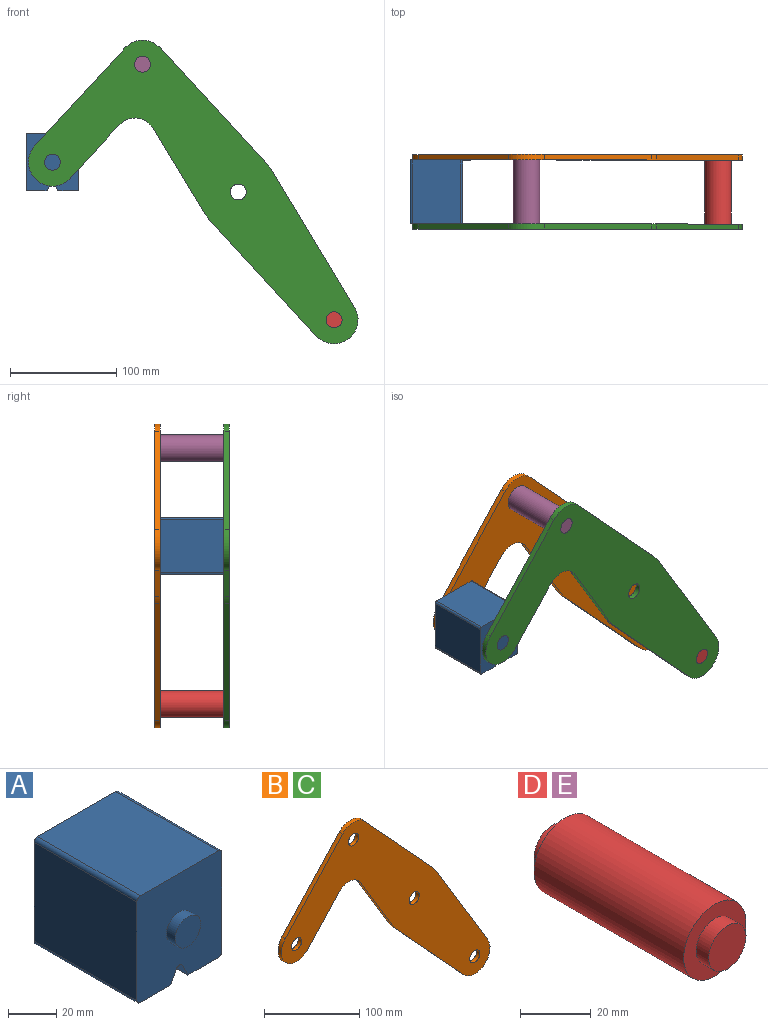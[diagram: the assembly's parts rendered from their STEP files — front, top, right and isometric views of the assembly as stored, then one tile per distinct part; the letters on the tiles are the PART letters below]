
ASSEMBLY  parts=5 mates=3
PART A: 18 faces, bbox 49.6x70x54 mm
  f0: plane 60x17.82mm, normal (0,0,-1), area 1069.2mm2, adj f4,f6,f10,f13
  f1: plane 60x50.01mm, normal (-1,0,0), area 3000.4mm2, adj f4,f10,f13,f14
  f2: plane 60x45.64mm, normal (0,0,1), area 2738.4mm2, adj f4,f10,f14,f15
  f3: plane 60x50.01mm, normal (1,0,0), area 3000.4mm2, adj f4,f10,f15,f16
  f4: plane 54.01x49.64mm, normal (0,-1,0), area 2454.3mm2, adj f0,f1,f2,f3,f5,f6,f7,f9
  f5: plane 60x17.82mm, normal (0,0,-1), area 1069.2mm2, adj f4,f7,f10,f16
  f6: plane 60x6.42mm, normal (0.89,0,-0.45), area 430.8mm2, adj f0,f4,f10,f17
  f7: plane 60x6.42mm, normal (-0.89,0,-0.45), area 430.8mm2, adj f4,f5,f10,f17
  f8: plane 15x15mm, normal (0,-1,0), area 176.7mm2, adj f9
  f9: cylinder r=7.5mm len=15mm, axis (0,1,0), area 235.6mm2, adj f4,f8
  f10: plane 54.01x49.64mm, normal (0,1,0), area 2454.3mm2, adj f0,f1,f2,f3,f5,f6,f7,f12
  f11: plane 15x15mm, normal (0,1,0), area 176.7mm2, adj f12
  f12: cylinder r=7.5mm len=15mm, axis (0,-1,0), area 235.6mm2, adj f10,f11
  f13: cylinder r=2mm len=60mm, axis (0,-1,0), area 188.5mm2, adj f0,f1,f4,f10
  f14: cylinder r=2mm len=60mm, axis (0,1,0), area 188.5mm2, adj f1,f2,f4,f10
  f15: cylinder r=2mm len=60mm, axis (0,-1,0), area 188.5mm2, adj f2,f3,f4,f10
  f16: cylinder r=2mm len=60mm, axis (0,1,0), area 188.5mm2, adj f3,f4,f5,f10
  f17: cylinder r=2mm len=60mm, axis (0,-1,0), area 265.7mm2, adj f4,f6,f7,f10
PART B: 18 faces, bbox 309.5x5x285.1 mm
  f0: cylinder r=37.5mm len=6mm, axis (0,1,0), area 37.6mm2, adj f1,f14,f16,f17
  f1: plane 109.88x101mm, normal (0.74,0,0.68), area 746.2mm2, adj f0,f2,f16,f17
  f2: cylinder r=22.5mm len=33.13mm, axis (0,1,0), area 186.2mm2, adj f1,f3,f16,f17
  f3: plane 92.03x84.59mm, normal (-0.74,0,0.68), area 625mm2, adj f2,f4,f16,f17
  f4: cylinder r=22.5mm len=39.07mm, axis (0,1,0), area 353.4mm2, adj f3,f5,f16,f17
  f5: plane 50.28x46.21mm, normal (0.74,0,-0.68), area 341.4mm2, adj f4,f6,f16,f17
  f6: cylinder r=20mm len=31.85mm, axis (0,1,0), area 185.5mm2, adj f5,f7,f16,f17
  f7: plane 79.23x47.81mm, normal (-0.86,0,-0.52), area 462.7mm2, adj f6,f8,f16,f17
  f8: cylinder r=37.5mm len=6mm, axis (0,1,0), area 37.6mm2, adj f7,f9,f16,f17
  f9: plane 109.88x101mm, normal (-0.74,0,-0.68), area 746.2mm2, adj f8,f10,f16,f17
  f10: cylinder r=22.5mm len=39.07mm, axis (0,1,0), area 330.9mm2, adj f9,f14,f16,f17
  f11: cylinder r=7.5mm len=15mm, axis (0,1,0), area 235.6mm2, adj f16,f17
  f12: cylinder r=7.5mm len=15mm, axis (0,1,0), area 235.6mm2, adj f16,f17
  f13: cylinder r=7.5mm len=15mm, axis (0,1,0), area 235.6mm2, adj f16,f17
  f14: plane 127.78x77.11mm, normal (0.86,0,0.52), area 746.2mm2, adj f0,f10,f16,f17
  f15: cylinder r=7.5mm len=15mm, axis (0,1,0), area 235.6mm2, adj f16,f17
  f16: plane 309.5x285.07mm, normal (0,-1,0), area 24555.4mm2, adj f0,f1,f2,f3,f4,f5,f6,f7
  f17: plane 309.5x285.07mm, normal (0,1,0), area 24555.4mm2, adj f0,f1,f2,f3,f4,f5,f6,f7
PART C: same geometry as B
PART D: 7 faces, bbox 25x70x25 mm
  f0: cylinder r=12.5mm len=60mm, axis (0,1,0), area 4712.4mm2, adj f1,f4
  f1: plane 25x25mm, normal (0,-1,0), area 314.2mm2, adj f0,f2
  f2: cylinder r=7.5mm len=15mm, axis (0,1,0), area 235.6mm2, adj f1,f3
  f3: plane 15x15mm, normal (0,-1,0), area 176.7mm2, adj f2
  f4: plane 25x25mm, normal (0,1,0), area 314.2mm2, adj f0,f5
  f5: cylinder r=7.5mm len=15mm, axis (0,-1,0), area 235.6mm2, adj f4,f6
  f6: plane 15x15mm, normal (0,1,0), area 176.7mm2, adj f5
PART E: same geometry as D
PLACE A t=(89.96,-30,-120.03)mm
PLACE B t=(89.96,35,-120.03)mm
PLACE C t=(89.96,-30,-120.03)mm fixed
PLACE D t=(269.87,-30,-360.1)mm
PLACE E t=(89.96,-30,-120.03)mm
MATE revolute A.f9 <-> C.f4  axis (0,-1,0) through (-174.54,-35,28)mm
MATE fastened B.f2 <-> E.f0  axis (0,-1,0) through (-89.96,30,120.03)mm
MATE fastened D.f0 <-> B.f13  axis (0,1,0) through (89.96,35,-120.03)mm
